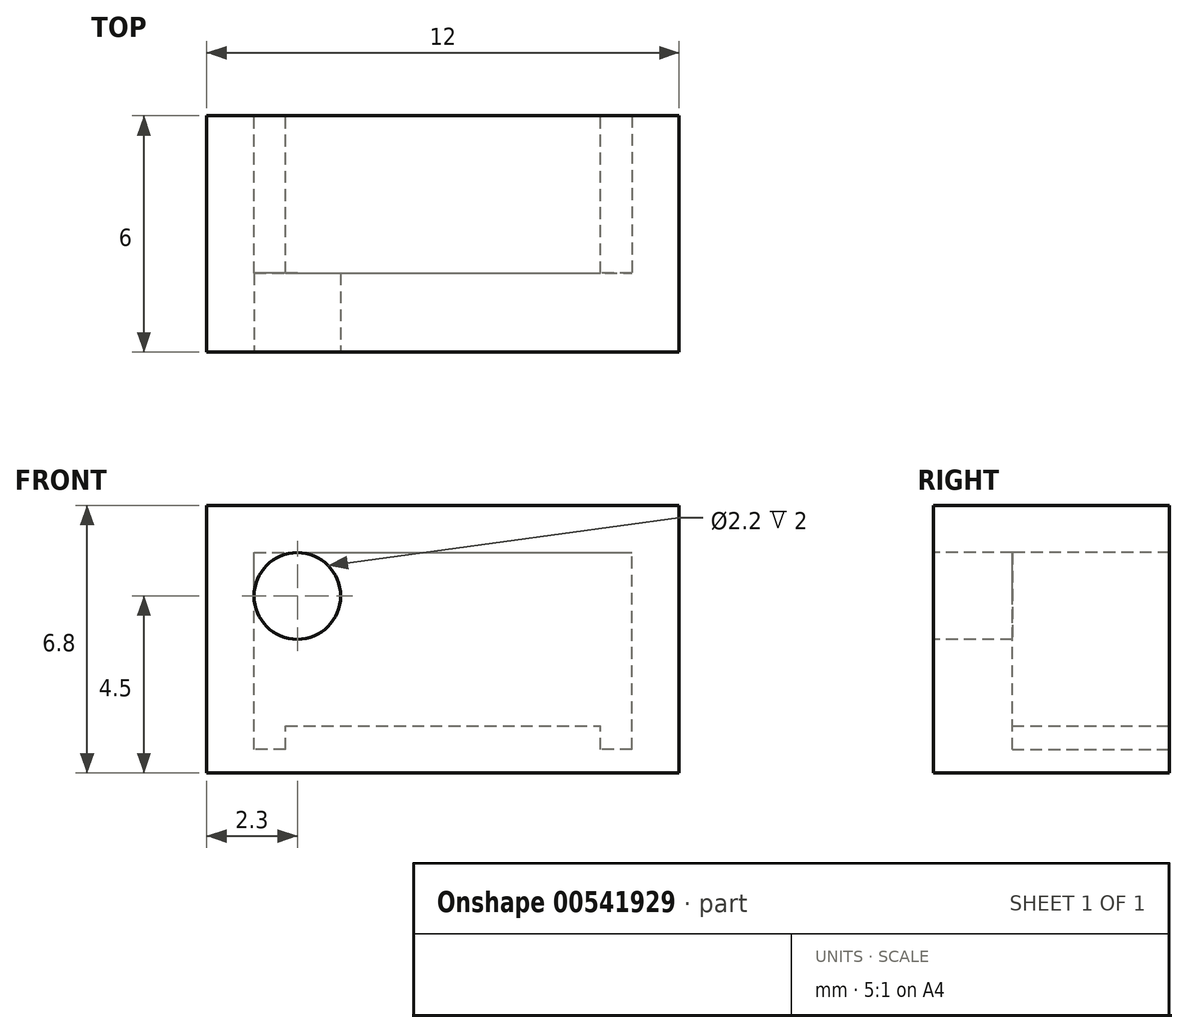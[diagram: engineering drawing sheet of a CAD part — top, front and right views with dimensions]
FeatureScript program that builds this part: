
annotation { "Feature Type Name" : "Feature", "Feature Type Description" : "" }
export const myFeature = defineFeature(function(context is Context, id is Id, definition is map)
    precondition{}
    {
        {
            var Q0;
            Q0=qCreatedBy(makeId("Front.planeOp"),FACE);
            var sketch = newSketch(context, id + "F0", { "sketchPlane" : qUnion([Q0])});
            skLineSegment(sketch, "E0.bottom", {"start": v(0, 0) * mm, "end": v(9.6, 0) * mm});
            skLineSegment(sketch, "E0.top", {"start": v(0, 4.4) * mm, "end": v(9.6, 4.4) * mm});
            skLineSegment(sketch, "E0.left", {"start": v(0, 0) * mm, "end": v(0, 4.4) * mm});
            skLineSegment(sketch, "E0.right", {"start": v(9.6, 0) * mm, "end": v(9.6, 4.4) * mm});
            skLineSegment(sketch, "E1.bottom", {"start": v(-1.2, -1.2) * mm, "end": v(10.8, -1.2) * mm});
            skLineSegment(sketch, "E1.top", {"start": v(-1.2, 5.6) * mm, "end": v(10.8, 5.6) * mm});
            skLineSegment(sketch, "E1.left", {"start": v(-1.2, -1.2) * mm, "end": v(-1.2, 5.6) * mm});
            skLineSegment(sketch, "E1.right", {"start": v(10.8, -1.2) * mm, "end": v(10.8, 5.6) * mm});
            skSolve(sketch);
        }
        {
            var Q0;
            Q0=makeQuery(id+"F0.imprint","IMPRINT",FACE,{"disambiguationData":[TD([[makeQuery(id+"F0.imprint","IMPRINT",EDGE,{"derivedFrom":sQuery(id+"F0.wireOp",EDGE,"E0.bottom")}),-1.0]])]});
            extrude(context, id + "F1", {"entities" : qUnion([Q0]), "oppositeDirection" : true, "depth" : 4 * mm, "offsetDistance" : 25 * mm, "hasSecondDirection" : true, "secondDirectionOppositeDirection" : false, "secondDirectionDepth" : 2 * mm});
        }
        {
            var Q0;
            Q0=makeQuery(id+"F1.opExtrude","SWEPT_FACE",FACE,{"disambiguationData":[OSD([sQuery(id+"F0.wireOp",EDGE,"E0.bottom")])]});
            var sketch = newSketch(context, id + "F2", { "sketchPlane" : qUnion([Q0])});
            skLineSegment(sketch, "E2.bottom", {"start": v(9.6, 0) * mm, "end": v(8.8, 0) * mm});
            skLineSegment(sketch, "E2.top", {"start": v(9.6, 4) * mm, "end": v(8.8, 4) * mm});
            skLineSegment(sketch, "E2.left", {"start": v(9.6, 0) * mm, "end": v(9.6, 4) * mm});
            skLineSegment(sketch, "E2.right", {"start": v(8.8, 0) * mm, "end": v(8.8, 4) * mm});
            skSolve(sketch);
        }
        {
            var Q0;
            {var subQ3=sQuery(id+"F2.wireOp",EDGE,"E2.top");Q0=makeQuery(id+"F2.imprint","IMPRINT",FACE,{"disambiguationData":[TD([[makeQuery(id+"F2.imprint","IMPRINT",EDGE,{"derivedFrom":subQ3}),-1.0]])]});}
            var sketch = newSketch(context, id + "F3", { "sketchPlane" : qUnion([Q0])});
            skLineSegment(sketch, "E3.bottom", {"start": v(0.8, 0) * mm, "end": v(0, 0) * mm});
            skLineSegment(sketch, "E3.top", {"start": v(0.8, 4) * mm, "end": v(0, 4) * mm});
            skLineSegment(sketch, "E3.left", {"start": v(0.8, 0) * mm, "end": v(0.8, 4) * mm});
            skLineSegment(sketch, "E3.right", {"start": v(0, 0) * mm, "end": v(0, 4) * mm});
            skSolve(sketch);
        }
        {
            var Q0;
            Q0=makeQuery(id+"F3.imprint","IMPRINT",FACE,{"disambiguationData":[TD([[makeQuery(id+"F3.imprint","IMPRINT",EDGE,{"derivedFrom":sQuery(id+"F3.wireOp",EDGE,"E3.bottom")}),-1.0]])]});
            var Q1;
            Q1=makeQuery(id+"F2.imprint","IMPRINT",FACE,{"disambiguationData":[TD([[makeQuery(id+"F2.imprint","IMPRINT",EDGE,{"derivedFrom":sQuery(id+"F2.wireOp",EDGE,"E2.bottom")}),-1.0]])]});
            extrude(context, id + "F4", {"entities" : qUnion([Q0, Q1]), "operationType" : NewBodyOperationType.REMOVE, "oppositeDirection" : true, "depth" : .6 * mm, "offsetDistance" : 25 * mm});
        }
        {
            var Q0;
            Q0=qCreatedBy(makeId("Front.planeOp"),FACE);
            var sketch = newSketch(context, id + "F5", { "sketchPlane" : qUnion([Q0])});
            skLineSegment(sketch, "E4.0", {"start": v(0, 0) * mm, "end": v(9.6, 0) * mm});
            skLineSegment(sketch, "E4.1", {"start": v(0, 4.4) * mm, "end": v(9.6, 4.4) * mm});
            skLineSegment(sketch, "E4.2", {"start": v(9.6, 0) * mm, "end": v(9.6, 4.4) * mm});
            skLineSegment(sketch, "E4.3", {"start": v(0, 0) * mm, "end": v(0, 4.4) * mm});
            skSolve(sketch);
        }
        {
            var Q0;
            Q0=makeQuery(id+"F5.imprint","IMPRINT",FACE,{"disambiguationData":[TD([[makeQuery(id+"F5.imprint","IMPRINT",EDGE,{"derivedFrom":sQuery(id+"F5.wireOp",EDGE,"E4.0")}),1.0]])]});
            extrude(context, id + "F6", {"entities" : qUnion([Q0]), "operationType" : NewBodyOperationType.ADD, "depth" : 2 * mm, "offsetDistance" : 25 * mm});
        }
        {
            var Q0;
            Q0=qCreatedBy(makeId("Front.planeOp"),FACE);
            var sketch = newSketch(context, id + "F7", { "sketchPlane" : qUnion([Q0])});
            skCircle(sketch, "E5", {"center": v(1.1, 3.3) * mm, "radius": 1.1 * mm});
            skSolve(sketch);
        }
        {
            var Q0;
            Q0=makeQuery(id+"F7.imprint","IMPRINT",FACE,{"disambiguationData":[TD([[makeQuery(id+"F7.imprint","IMPRINT",EDGE,{"derivedFrom":sQuery(id+"F7.wireOp",EDGE,"E5")}),1.0]])]});
            extrude(context, id + "F8", {"entities" : qUnion([Q0]), "operationType" : NewBodyOperationType.REMOVE, "oppositeDirection" : true, "depth" : 25 * mm, "offsetDistance" : 25 * mm, "symmetric" : true});
        }
    });
